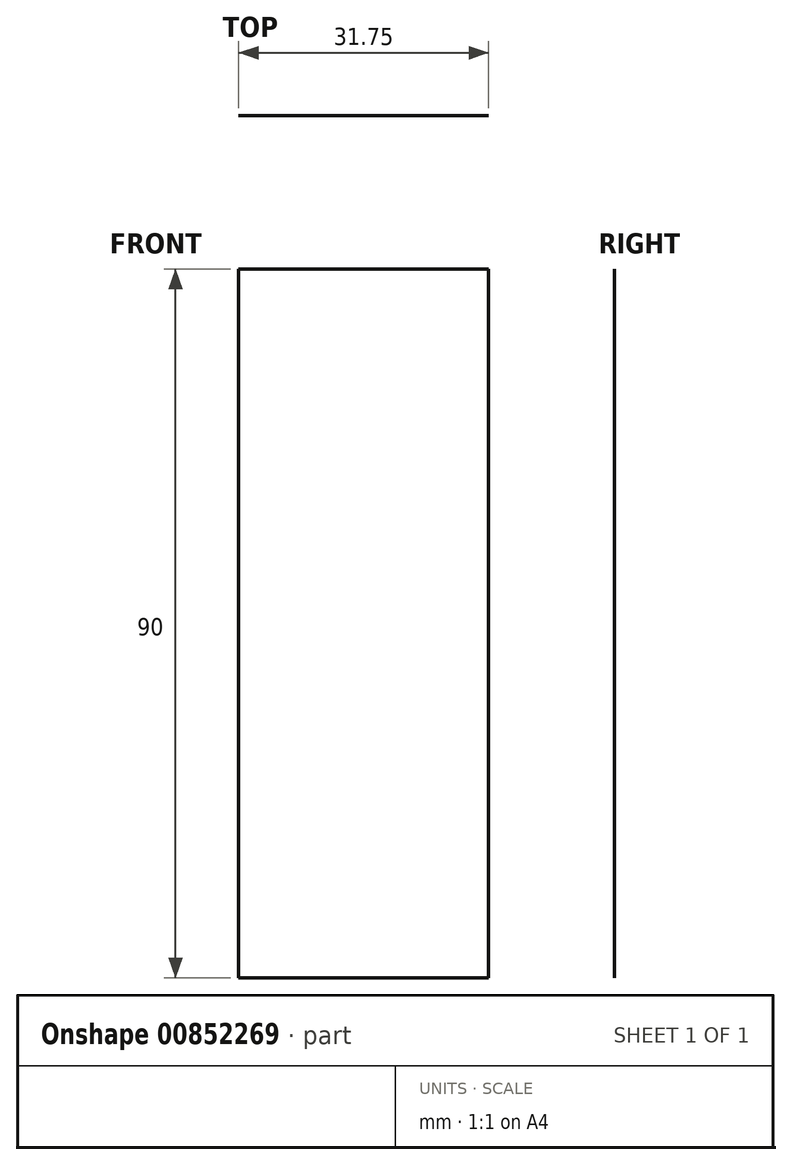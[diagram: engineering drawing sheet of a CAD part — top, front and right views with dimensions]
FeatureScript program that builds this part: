
annotation { "Feature Type Name" : "Feature", "Feature Type Description" : "" }
export const myFeature = defineFeature(function(context is Context, id is Id, definition is map)
    precondition{}
    {
        {
            var Q0;
            Q0=qCreatedBy(makeId("Front.planeOp"),FACE);
            var sketch = newSketch(context, id + "F0", { "sketchPlane" : qUnion([Q0])});
            skLineSegment(sketch, "E0.bottom", {"start": v(0, 0) * mm, "end": v(31.75, 0) * mm});
            skLineSegment(sketch, "E0.top", {"start": v(0, -90) * mm, "end": v(31.75, -90) * mm});
            skLineSegment(sketch, "E0.left", {"start": v(0, 0) * mm, "end": v(0, -90) * mm});
            skLineSegment(sketch, "E0.right", {"start": v(31.75, 0) * mm, "end": v(31.75, -90) * mm});
            skSolve(sketch);
        }
        {
            var Q0;
            Q0=makeQuery(id+"F0.imprint","IMPRINT",FACE,{"disambiguationData":[TD([[makeQuery(id+"F0.imprint","IMPRINT",EDGE,{"derivedFrom":sQuery(id+"F0.wireOp",EDGE,"E0.bottom")}),-1.0]])]});
            extrude(context, id + "F1", {"entities" : qUnion([Q0]), "depth" : 1 / 203.2 * mm, "offsetDistance" : 25.4 * mm});
        }
    });
